# Revit family: QF_BOURGEAT_chariot_petit_dejeuner_modele_glissieres_polypropylene_2niveaux
name_source: partatom
category: Equipement spécialisé
revit_build: Autodesk Revit 2015 (Build: 20140606_1530(x64)
units: mm (PartAtom-declared; Revit-internal decimal feet)

## types (4) — shared parameters
Charge max = 120.00 kg
Fabricant = BOURGEAT
Hauteur hors tout = 1055 mm  [stored 3.46129 ft]
Longueur hors tout = 925 mm  [stored 3.03478 ft]
Profondeur hors tout = 620 mm  [stored 2.03412 ft]
Spécification du Fabricant = CHARIOT PETIT DEJEUNER A GLISSIERE INOX DOUBLE ENTREE 325mm
URL catalogue = http://www.bourgeat.fr

## per-type parameters (varying)
| type | Modèle | Poids net à vide | panneaux_lateraux | tablette rabatable(789510) |
| chariot_petit_dejeuner_glissiere_polypropylene_sans_panneaux | 788406 | 25.00 kg | Non | Non |
| chariot_petit_dejeuner_glissiere_polypropylene_sans_panneaux+tablette | 788406+789510 | 25.00 kg | Non | Oui |
| chariot_petit_dejeuner_glissiere_polypropylene_avec_panneaux | 788306 | 27.50 kg | Oui | Non |
| chariot_petit_dejeuner_glissiere_polypropylene_avec_panneaux+tablette | 788306 + 789510 | 27.50 kg | Oui | Oui |

note: [stored X ft] marks values corroborated as IEEE doubles in the binary element streams (Revit-internal decimal feet)
